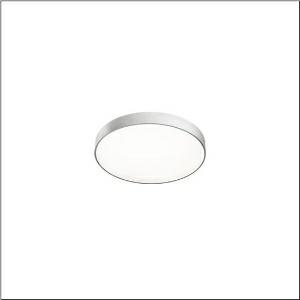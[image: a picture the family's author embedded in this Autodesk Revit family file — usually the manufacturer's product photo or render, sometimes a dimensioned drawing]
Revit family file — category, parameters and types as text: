
# Revit family: round_21_s_51mr34gd0421s
name_source: partatom
category: Lighting Fixtures
units: mm (PartAtom-declared; Revit-internal decimal feet)

## family parameters
Cut with Voids When Loaded = No
Host = Face
Light Source = No
Part Type = Normal
Room Calculation Point = No
Round Connector Dimension = Use Diameter
Shared = No

## types (1)
- Round 21 S (1 x LED, 4090 lm, 28.3 W, 4000K)
    Apparent Load = 28 VA
    CIE Flux Codes = 49 80 96 79 100
    Color Rendering = 80
    Color Temperature = 4000K
    Default Elevation = 1800 mm
    Description = Round 21 S, wall and ceiling luminaire, primary optical cover: cover, of PMMA, opal, light emission: direct/indirect distribution, primary light characteristic: symmetric, installation type: suspended mounting, surface-mounted, LED, rated luminous flux: 4.090lm, luminous efficacy: 135lm/W, light colour: 840, colour temperature: 4000K, control gear: DALI 2, with terminal, 5-pole, mains connection: 230V, AC, 50/60Hz, rated input power: 28.3W, housing, of aluminium, coated, silver, diameter: 400mm, height: 62mm, protection rating (complete): IP40, insulation class (complete): insulation class I (protective earthing), certification: CE, impact resistance: IK04, permissible operating ambient temperature: -10..+35°C, packaging unit: 1 piece
    Height = 87 mm
    Lamp = 1 x LED
    Lamp Light Flux = 4090 lm
    Lamp Power = 28.3 W
    Lamp count = 1
    Length = 400 mm
    Luminous efficacy = 145 lm/W
    Manufacturer = Siteco
    ModVariant = No
    Model = 51MR34GD0421S
    Mounting Place = Ceiling
    Mounting Type = Surface mounted
    Number of Poles = 1
    OnlyDefault = Yes
    Power Factor = 1
    Product Name = Round 21 S
    Product group = wall and ceiling luminaire
    ProductGroupID = 304
    Protection Class = Protection class I
    Protection Degree = IP 40
    RLX_Detail_Level = 1
    RLX_Emergency_Light_Flux = 0 lm
    RLX_Emergency_Type = 0
    RLX_Emergency_Type_DB = No
    RlxData = <blob elided: 11565 chars, md5=d6f7e4a6>
    Socket = socket
    Standby Power = 0 W
    System Light Flux = 4090 lm
    System Power = 28 W
    Type Comments = Product without accessories
    Type Image = l_1258309.jpg
    URL = http://relux.com
    VarID = ---
    Voltage = 0 V
    Weight = 0.00 kg
    Width = 0 mm  [stored 0 ft]

note: [stored X ft] marks values corroborated as IEEE doubles in the binary element streams (Revit-internal decimal feet)

## geometry (parser evidence)
native form markers: Sweep x12
no freeform markers — native parametric forms only
